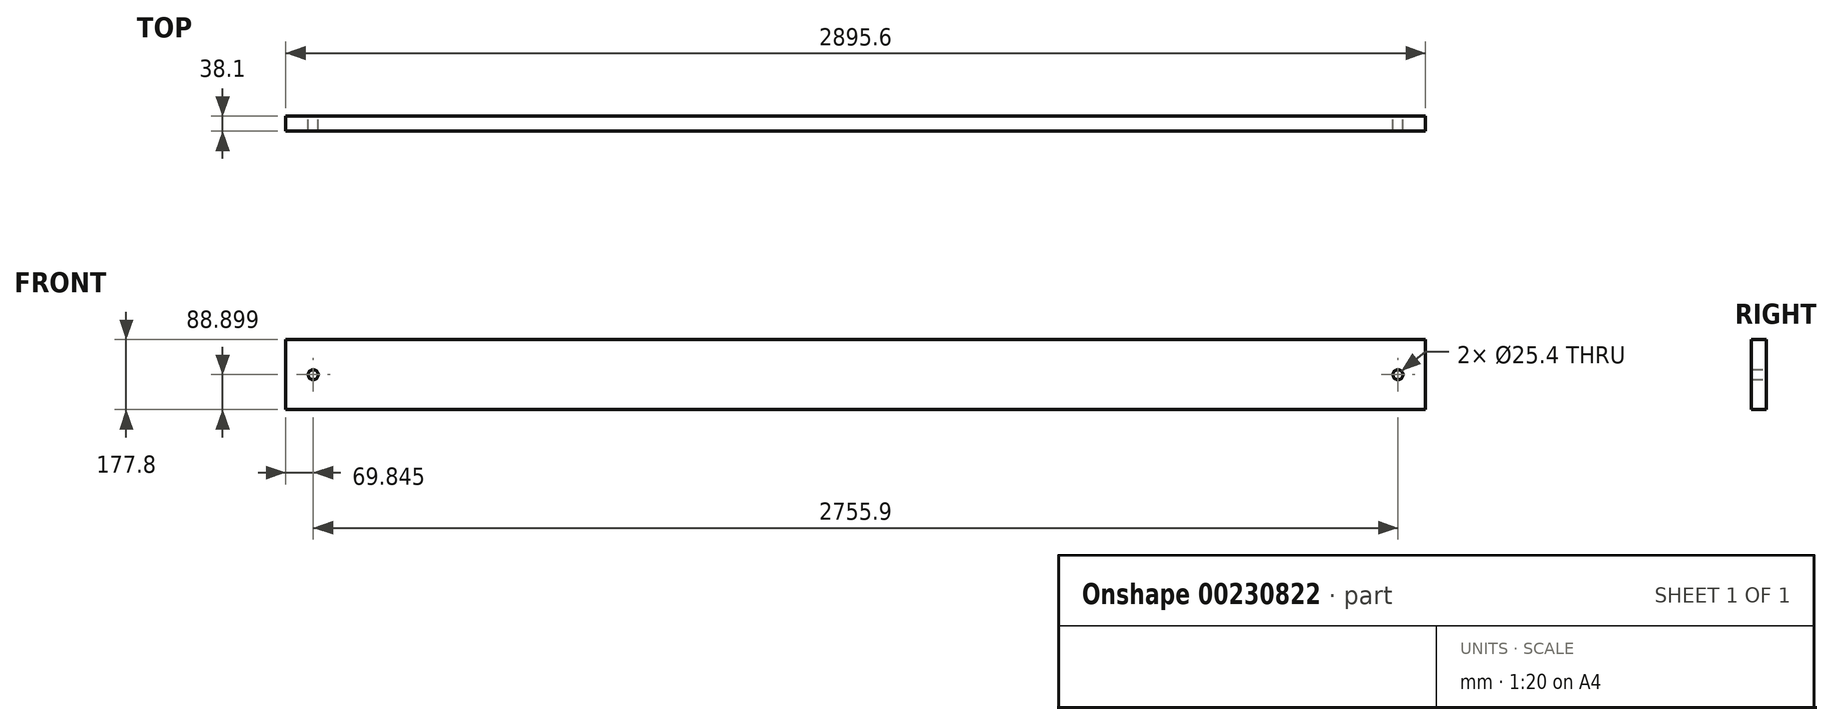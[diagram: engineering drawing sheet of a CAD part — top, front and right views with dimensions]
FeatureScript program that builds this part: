
annotation { "Feature Type Name" : "Feature", "Feature Type Description" : "" }
export const myFeature = defineFeature(function(context is Context, id is Id, definition is map)
    precondition{}
    {
        {
            var Q0;
            Q0=qCreatedBy(makeId("Front.planeOp"),FACE);
            var sketch = newSketch(context, id + "F0", { "sketchPlane" : qUnion([Q0])});
            skLineSegment(sketch, "E0.bottom", {"start": v(-1459.82, 23.6) * mm, "end": v(1435.78, 23.6) * mm});
            skLineSegment(sketch, "E0.top", {"start": v(-1459.82, -154.2) * mm, "end": v(1435.78, -154.2) * mm});
            skLineSegment(sketch, "E0.left", {"start": v(-1459.82, 23.6) * mm, "end": v(-1459.82, -154.2) * mm});
            skLineSegment(sketch, "E0.right", {"start": v(1435.78, 23.6) * mm, "end": v(1435.78, -154.2) * mm});
            skCircle(sketch, "E1", {"center": v(1365.93, -65.3) * mm, "radius": 12.7 * mm});
            skCircle(sketch, "E2", {"center": v(-1389.97, -65.3) * mm, "radius": 12.7 * mm});
            skSolve(sketch);
        }
        {
            var Q0;
            Q0=makeQuery(id+"F0.imprint","IMPRINT",FACE,{"disambiguationData":[TD([[makeQuery(id+"F0.imprint","IMPRINT",EDGE,{"derivedFrom":sQuery(id+"F0.wireOp",EDGE,"E0.bottom")}),-1.0]])]});
            extrude(context, id + "F1", {"entities" : qUnion([Q0]), "depth" : 38.1 * mm});
        }
    });
